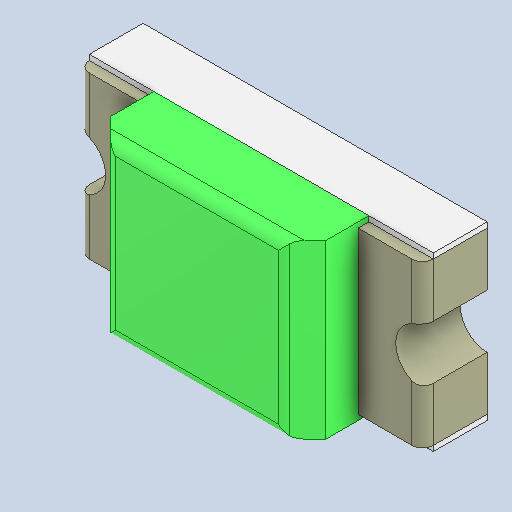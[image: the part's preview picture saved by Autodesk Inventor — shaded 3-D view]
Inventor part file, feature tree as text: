
AUTODESK INVENTOR PART (.ipt)
format: ipt  version: 2022 (Build 260153000, 153)  size: 159,232 bytes
history: native  units: in
note: dims shown in document units (in); Inventor stores cm internally (conversion verified against a paired STEP export)
features: fillet x2, other x2
ambient origin geometry x8: Origin, YZ Plane, XZ Plane, XY Plane, X Axis, Y Axis, Z Axis, Center Point
bodies: Solid1 (feature_tree), Solid2 (feature_tree), Solid3 (feature_tree), Solid4 (feature_tree)
feature tree (4):
  fillet  "Fillet001_(Solid)001:1"  [1 undecoded]
  fillet  "Fillet001_(Solid):1"  [1 undecoded]
  other  "Lens:1"
  other  "Base:1"
note: 2 required parameter values undecoded (feature->parameter linkage not recoverable at this tier; creation-order binding heuristic only, values carry confidence <= 0.55)
